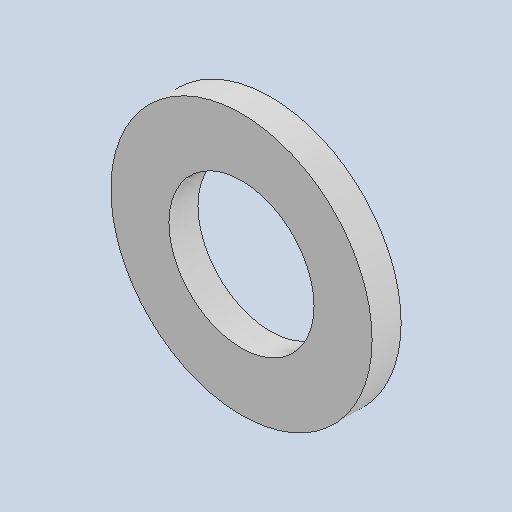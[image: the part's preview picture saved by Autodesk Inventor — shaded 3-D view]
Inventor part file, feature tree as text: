
AUTODESK INVENTOR PART (.ipt)
format: ipt  version: 2023 (Build 270158000, 158)  size: 137,728 bytes
history: native  units: in
note: dims shown in document units (in); Inventor stores cm internally (conversion verified against a paired STEP export)
features: extrude x1, sketch x1
ambient origin geometry x8: Origin, YZ Plane, XZ Plane, XY Plane, X Axis, Y Axis, Z Axis, Center Point
bodies: Solid1 (feature_tree)
feature tree (2):
  extrude  "Extrusion1"  Depth=0.0394in
  sketch  "Sketch1"  dims[d0=0.1969in d1=0.3543in d2=0.0394in d3=0.0in]
